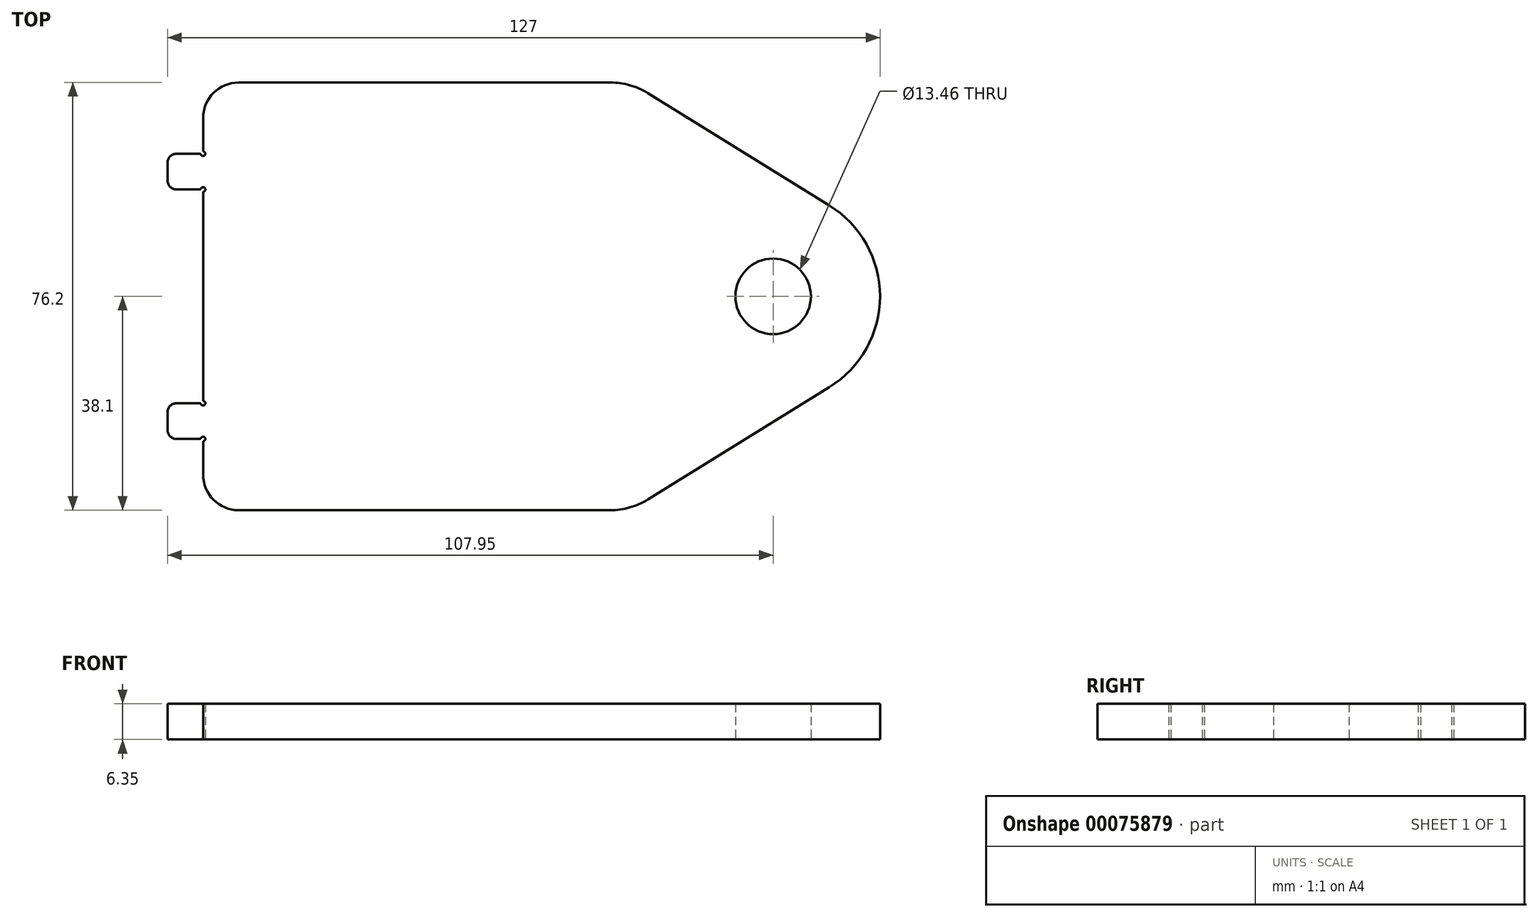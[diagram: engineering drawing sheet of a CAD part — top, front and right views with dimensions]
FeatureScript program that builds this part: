
annotation { "Feature Type Name" : "Feature", "Feature Type Description" : "" }
export const myFeature = defineFeature(function(context is Context, id is Id, definition is map)
    precondition{}
    {
        {
            var Q0;
            Q0=qCreatedBy(makeId("Top.planeOp"),FACE);
            var sketch = newSketch(context, id + "F0", { "sketchPlane" : qUnion([Q0])});
            skLineSegment(sketch, "E0.bottom", {"start": v(34.5, 38.1) * mm, "end": v(-31.75, 38.1) * mm});
            skLineSegment(sketch, "E0.top", {"start": v(34.5, -38.1) * mm, "end": v(-31.75, -38.1) * mm});
            skLineSegment(sketch, "E0.right", {"start": v(-38.1, 31.75) * mm, "end": v(-38.1, 26.03) * mm});
            skPoint(sketch, "E0.middle", {"position": v(0, 0) * mm});
            skLineSegment(sketch, "E1", {"start": v(41.17, 36.2) * mm, "end": v(73.52, 16.2) * mm});
            skLineSegment(sketch, "E2", {"start": v(73.52, -16.2) * mm, "end": v(41.17, -36.2) * mm});
            skPoint(sketch, "E3.visualSharp", {"position": v(99.73, 0) * mm});
            skArc(sketch, "E3.filletArc", {"start": v(73.52, -16.2) * mm, "mid": v(82.55, 0) * mm, "end": v(73.52, 16.2) * mm});
            skPoint(sketch, "E4.visualSharp", {"position": v(38.1, 38.1) * mm});
            skArc(sketch, "E4.filletArc", {"start": v(41.17, 36.2) * mm, "mid": v(37.96, 37.62) * mm, "end": v(34.5, 38.1) * mm});
            skPoint(sketch, "E5.visualSharp", {"position": v(38.1, -38.1) * mm});
            skArc(sketch, "E5.filletArc", {"start": v(34.5, -38.1) * mm, "mid": v(37.96, -37.62) * mm, "end": v(41.17, -36.2) * mm});
            skPoint(sketch, "E6.visualSharp", {"position": v(-38.1, 38.1) * mm});
            skArc(sketch, "E6.filletArc", {"start": v(-31.75, 38.1) * mm, "mid": v(-36.24, 36.24) * mm, "end": v(-38.1, 31.75) * mm});
            skPoint(sketch, "E7.visualSharp", {"position": v(-38.1, -38.1) * mm});
            skArc(sketch, "E7.filletArc", {"start": v(-38.1, -31.75) * mm, "mid": v(-36.24, -36.24) * mm, "end": v(-31.75, -38.1) * mm});
            skLineSegment(sketch, "E8.bottom", {"start": v(-38.73, 25.4) * mm, "end": v(-42.86, 25.4) * mm});
            skLineSegment(sketch, "E8.top", {"start": v(-38.73, 19.05) * mm, "end": v(-42.86, 19.05) * mm});
            skLineSegment(sketch, "E8.right", {"start": v(-44.45, 23.81) * mm, "end": v(-44.45, 20.64) * mm});
            skLineSegment(sketch, "E9.MirrorCS", {"start": v(-38.73, -19.05) * mm, "end": v(-42.86, -19.05) * mm});
            skLineSegment(sketch, "E10.MirrorCS", {"start": v(-44.45, -23.81) * mm, "end": v(-44.45, -20.64) * mm});
            skLineSegment(sketch, "E11.MirrorCS", {"start": v(-38.73, -25.4) * mm, "end": v(-42.86, -25.4) * mm});
            skLineSegment(sketch, "E12.trimOffspring", {"start": v(-38.1, 18.42) * mm, "end": v(-38.1, -18.42) * mm});
            skLineSegment(sketch, "E13.trimOffspring", {"start": v(-38.1, -26.03) * mm, "end": v(-38.1, -31.75) * mm});
            skPoint(sketch, "E14.visualSharp", {"position": v(-44.45, 25.4) * mm});
            skArc(sketch, "E14.filletArc", {"start": v(-42.86, 25.4) * mm, "mid": v(-43.99, 24.94) * mm, "end": v(-44.45, 23.81) * mm});
            skPoint(sketch, "E15.visualSharp", {"position": v(-44.45, 19.05) * mm});
            skArc(sketch, "E15.filletArc", {"start": v(-44.45, 20.64) * mm, "mid": v(-43.99, 19.51) * mm, "end": v(-42.86, 19.05) * mm});
            skPoint(sketch, "E16.visualSharp", {"position": v(-44.45, -19.05) * mm});
            skArc(sketch, "E16.filletArc", {"start": v(-42.86, -19.05) * mm, "mid": v(-43.99, -19.51) * mm, "end": v(-44.45, -20.64) * mm});
            skPoint(sketch, "E17.visualSharp", {"position": v(-44.45, -25.4) * mm});
            skArc(sketch, "E17.filletArc", {"start": v(-44.45, -23.81) * mm, "mid": v(-43.99, -24.94) * mm, "end": v(-42.86, -25.4) * mm});
            skArc(sketch, "E18", {"start": v(-38.46, 25.23) * mm, "mid": v(-37.82, 25.12) * mm, "end": v(-37.93, 25.76) * mm});
            skArc(sketch, "E19", {"start": v(-37.93, 18.7) * mm, "mid": v(-37.82, 19.33) * mm, "end": v(-38.46, 19.22) * mm});
            skArc(sketch, "E20.MirrorC", {"start": v(-38.46, -25.23) * mm, "mid": v(-37.82, -25.12) * mm, "end": v(-37.93, -25.76) * mm});
            skArc(sketch, "E21.MirrorC", {"start": v(-37.93, -18.7) * mm, "mid": v(-37.82, -19.33) * mm, "end": v(-38.46, -19.22) * mm});
            skPoint(sketch, "E22.visualSharp", {"position": v(-38.1, 25.8) * mm});
            skArc(sketch, "E22.filletArc", {"start": v(-38.1, 26.03) * mm, "mid": v(-38.05, 25.87) * mm, "end": v(-37.93, 25.76) * mm});
            skPoint(sketch, "E23.visualSharp", {"position": v(-38.5, 25.4) * mm});
            skArc(sketch, "E23.filletArc", {"start": v(-38.46, 25.23) * mm, "mid": v(-38.57, 25.35) * mm, "end": v(-38.73, 25.4) * mm});
            skPoint(sketch, "E24.visualSharp", {"position": v(-38.5, 19.05) * mm});
            skArc(sketch, "E24.filletArc", {"start": v(-38.73, 19.05) * mm, "mid": v(-38.57, 19.1) * mm, "end": v(-38.46, 19.22) * mm});
            skPoint(sketch, "E25.visualSharp", {"position": v(-38.1, 18.65) * mm});
            skArc(sketch, "E25.filletArc", {"start": v(-37.93, 18.7) * mm, "mid": v(-38.05, 18.58) * mm, "end": v(-38.1, 18.42) * mm});
            skPoint(sketch, "E26.visualSharp", {"position": v(-38.5, -25.4) * mm});
            skArc(sketch, "E26.filletArc", {"start": v(-38.73, -25.4) * mm, "mid": v(-38.57, -25.35) * mm, "end": v(-38.46, -25.23) * mm});
            skPoint(sketch, "E27.visualSharp", {"position": v(-38.1, -25.8) * mm});
            skArc(sketch, "E27.filletArc", {"start": v(-37.93, -25.76) * mm, "mid": v(-38.05, -25.87) * mm, "end": v(-38.1, -26.03) * mm});
            skPoint(sketch, "E28.visualSharp", {"position": v(-38.1, -18.65) * mm});
            skArc(sketch, "E28.filletArc", {"start": v(-38.1, -18.42) * mm, "mid": v(-38.05, -18.58) * mm, "end": v(-37.93, -18.7) * mm});
            skPoint(sketch, "E29.visualSharp", {"position": v(-38.5, -19.05) * mm});
            skArc(sketch, "E29.filletArc", {"start": v(-38.46, -19.22) * mm, "mid": v(-38.57, -19.1) * mm, "end": v(-38.73, -19.05) * mm});
            skCircle(sketch, "E30", {"center": v(63.5, 0) * mm, "radius": 6.73 * mm});
            skSolve(sketch);
        }
        {
            var Q0;
            Q0 = qSketchRegion(id + "F0", true);
            extrude(context, id + "F1", {"entities" : qUnion([Q0]), "depth" : 6.35 * mm});
        }
    });
